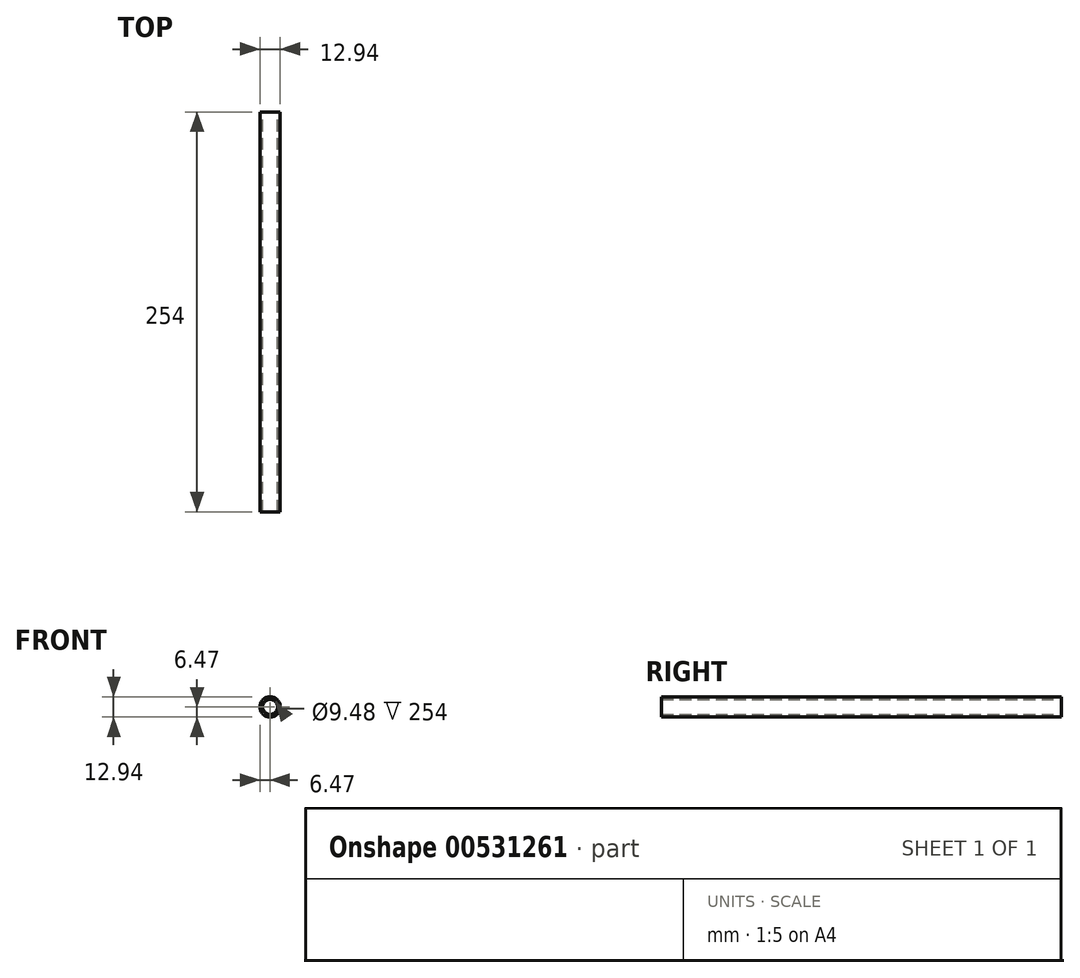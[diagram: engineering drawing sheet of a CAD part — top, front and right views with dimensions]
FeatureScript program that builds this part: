
annotation { "Feature Type Name" : "Feature", "Feature Type Description" : "" }
export const myFeature = defineFeature(function(context is Context, id is Id, definition is map)
    precondition{}
    {
        {
            var Q0;
            Q0=qCreatedBy(makeId("Front.planeOp"),FACE);
            var sketch = newSketch(context, id + "F0", { "sketchPlane" : qUnion([Q0])});
            skCircle(sketch, "E0", {"center": v(0, 0) * mm, "radius": 6.47 * mm});
            skCircle(sketch, "E1", {"center": v(0, 0) * mm, "radius": 4.74 * mm});
            skSolve(sketch);
        }
        {
            var Q0;
            Q0=makeQuery(id+"F0.imprint","IMPRINT",FACE,{"disambiguationData":[TD([[makeQuery(id+"F0.imprint","IMPRINT",EDGE,{"derivedFrom":sQuery(id+"F0.wireOp",EDGE,"E0")}),1.0]])]});
            extrude(context, id + "F1", {"entities" : qUnion([Q0]), "depth" : 254 * mm, "offsetDistance" : 25.4 * mm});
        }
    });
